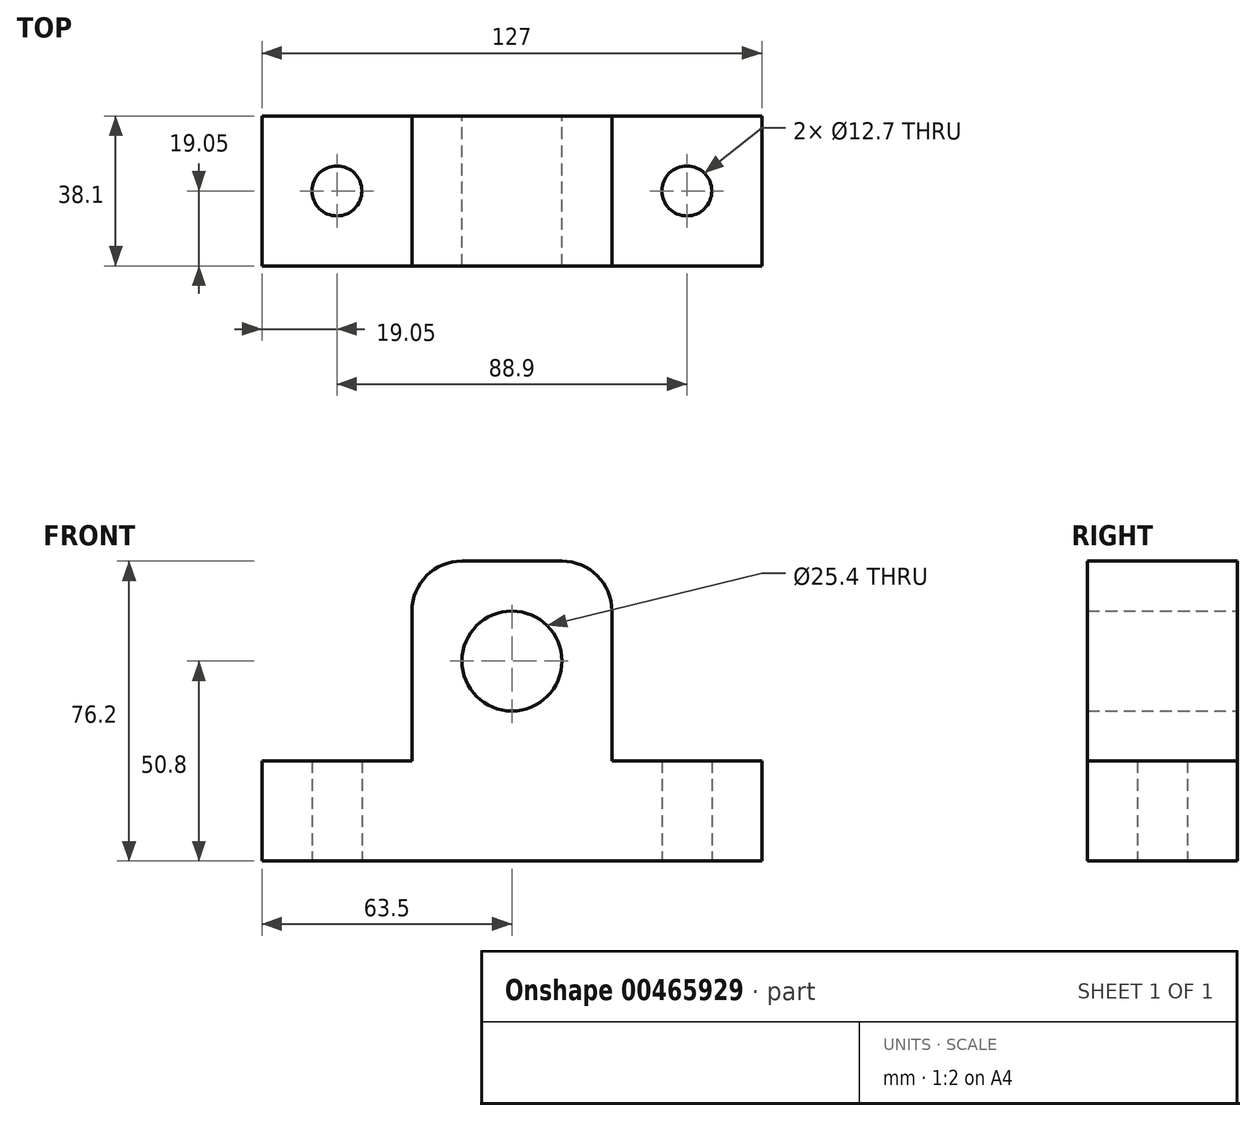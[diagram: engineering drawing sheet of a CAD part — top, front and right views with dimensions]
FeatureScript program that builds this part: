
annotation { "Feature Type Name" : "Feature", "Feature Type Description" : "" }
export const myFeature = defineFeature(function(context is Context, id is Id, definition is map)
    precondition{}
    {
        {
            var Q0;
            Q0=qCreatedBy(makeId("Front.planeOp"),FACE);
            var sketch = newSketch(context, id + "F0", { "sketchPlane" : qUnion([Q0])});
            skLineSegment(sketch, "E0.bottom", {"start": v(-63.5, 12.7) * mm, "end": v(63.5, 12.7) * mm});
            skLineSegment(sketch, "E0.top", {"start": v(-63.5, -12.7) * mm, "end": v(63.5, -12.7) * mm});
            skLineSegment(sketch, "E0.left", {"start": v(-63.5, 12.7) * mm, "end": v(-63.5, -12.7) * mm});
            skLineSegment(sketch, "E0.right", {"start": v(63.5, 12.7) * mm, "end": v(63.5, -12.7) * mm});
            skPoint(sketch, "E0.middle", {"position": v(0, 0) * mm});
            skLineSegment(sketch, "E1", {"start": v(0, 12.7) * mm, "end": v(-25.4, 12.7) * mm});
            skLineSegment(sketch, "E2", {"start": v(-25.4, 12.7) * mm, "end": v(25.4, 12.7) * mm});
            skLineSegment(sketch, "E3", {"start": v(25.4, 12.7) * mm, "end": v(25.4, 63.5) * mm});
            skLineSegment(sketch, "E4", {"start": v(25.4, 63.5) * mm, "end": v(-25.4, 63.5) * mm});
            skLineSegment(sketch, "E5", {"start": v(-25.4, 63.5) * mm, "end": v(-25.4, 12.7) * mm});
            skLineSegment(sketch, "E6", {"start": v(0, 63.5) * mm, "end": v(0, 38.1) * mm});
            skPoint(sketch, "E6.endSnap0", {"position": v(0, 63.5) * mm});
            skCircle(sketch, "E7", {"center": v(0, 38.1) * mm, "radius": 12.7 * mm});
            skSolve(sketch);
        }
        {
            var Q0;
            Q0=makeQuery(id+"F0.imprint","IMPRINT",FACE,{"disambiguationData":[TD([[makeQuery(id+"F0.imprint","IMPRINT",EDGE,{"derivedFrom":sQuery(id+"F0.wireOp",EDGE,"E0.top")}),1.0]])]});
            var Q1;
            {var subQ1=sQuery(id+"F0.wireOp",EDGE,"E3");Q1=makeQuery(id+"F0.imprint","IMPRINT",FACE,{"disambiguationData":[TD([[makeQuery(id+"F0.imprint","IMPRINT",EDGE,{"derivedFrom":subQ1}),1.0]])]});}
            extrude(context, id + "F1", {"entities" : qUnion([Q0, Q1]), "endBound" : BoundingType.SYMMETRIC, "depth" : 38.1 * mm});
        }
        {
            var Q0;
            Q0=makeQuery(id+"F1.opExtrude","SWEPT_EDGE",EDGE,{"disambiguationData":[OSD([sQuery(id+"F0.wireOp",EDGE,"E4"),sQuery(id+"F0.wireOp",EDGE,"E5")])]});
            var Q1;
            Q1=makeQuery(id+"F1.opExtrude","SWEPT_EDGE",EDGE,{"disambiguationData":[OSD([sQuery(id+"F0.wireOp",EDGE,"E3"),sQuery(id+"F0.wireOp",EDGE,"E4")])]});
            fillet(context, id + "F2", {"entities" : qUnion([Q0, Q1]), "radius" : 12.7 * mm, "tangentPropagation" : true, "allowEdgeOverflow" : false});
        }
        {
            var Q0;
            {var subQ0=sQuery(id+"F0.wireOp",EDGE,"E0.bottom");Q0=makeQuery(id+"F1.opExtrude","SWEPT_FACE",FACE,{"disambiguationData":[OSD([subQ0]),TDD([makeQuery(id+"F0.imprint","IMPRINT",EDGE,{"disambiguationData":[TD([[makeQuery(id+"F0.imprint","INTERSECT",VERTEX,{"derivedFrom":[subQ0,sQuery(id+"F0.wireOp",EDGE,"E0.left")]}),-1.0]])],"derivedFrom":subQ0})])]});}
            var sketch = newSketch(context, id + "F3", { "sketchPlane" : qUnion([Q0])});
            skLineSegment(sketch, "E8", {"start": v(-63.5, 0) * mm, "end": v(-44.45, 0) * mm});
            skPoint(sketch, "E8.endSnap0", {"position": v(-63.5, 0) * mm});
            skCircle(sketch, "E9", {"center": v(-44.45, 0) * mm, "radius": 6.35 * mm});
            skLineSegment(sketch, "E10", {"start": v(0, 0) * mm, "end": v(44.45, 0) * mm});
            skCircle(sketch, "E11", {"center": v(44.45, 0) * mm, "radius": 6.35 * mm});
            skSolve(sketch);
        }
        {
            var Q0;
            Q0=makeQuery(id+"F3.imprint","IMPRINT",FACE,{"disambiguationData":[TD([[makeQuery(id+"F3.imprint","IMPRINT",EDGE,{"derivedFrom":sQuery(id+"F3.wireOp",EDGE,"E11")}),1.0]])]});
            var Q1;
            Q1=makeQuery(id+"F3.imprint","IMPRINT",FACE,{"disambiguationData":[TD([[makeQuery(id+"F3.imprint","IMPRINT",EDGE,{"derivedFrom":sQuery(id+"F3.wireOp",EDGE,"E9")}),1.0]])]});
            extrude(context, id + "F4", {"entities" : qUnion([Q0, Q1]), "operationType" : NewBodyOperationType.REMOVE, "endBound" : BoundingType.SYMMETRIC, "depth" : 50.8 * mm});
        }
    });
